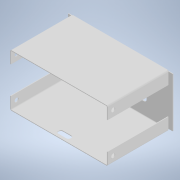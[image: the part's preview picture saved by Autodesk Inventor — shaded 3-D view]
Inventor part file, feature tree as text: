
AUTODESK INVENTOR PART (.ipt)
format: ipt  version: 2022 (Build 260153000, 153)  size: 239,104 bytes
history: native  units: mm
features: other x21, reference x11, sketch x7, mirror x1
ambient origin geometry x8: Origin, YZ Plane, XZ Plane, XY Plane, X Axis, Y Axis, Z Axis, Center Point
bodies: Body1 (feature_tree)
feature tree (40):
  other  "Твердое тело1"
  other  "РабПлоскость1"
  other  "Грань1"
  other  "Фланец1"
  mirror  "Зеркальное отражение1"
  other  "УглСкругление1"
  other  "Фланец3"
  sketch  "Эскиз1"
  other  "Пластина1"
  sketch  "Эскиз2"
  other  "Пластина2"
  other  "Сгиб1"
  other  "УглСтык1"
  sketch  "Эскиз3"
  sketch  "Эскиз4"
  sketch  "Эскиз5"
  reference  "Ссылка1"
  reference  "Ссылка2"
  reference  "Ссылка3"
  reference  "Ссылка4"
  reference  "Ссылка5"
  reference  "Ссылка6"
  reference  "Ссылка7"
  reference  "Ссылка8"
  reference  "Ссылка9"
  sketch  "Эскиз12"
  other  "Пластина4"
  other  "Сгиб3"
  other  "УглСтык3"
  sketch  "Эскиз13"
  reference  "Ссылка12"
  reference  "Ссылка13"
  other  "Вырез1"
  other  "Вырез2"
  other  "Вырез3"
  other  "Вырез6"
  other  "<userpath>\Documents\Git\MZCAT_battery\FastBattery2.iam"
  other  "FastBattery2.iam"
  other  "xb-acf005-2r:1"
  other  "akkum_base2_2:1"
